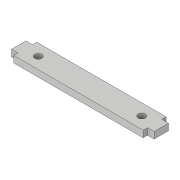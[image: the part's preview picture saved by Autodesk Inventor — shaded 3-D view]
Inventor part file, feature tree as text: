
AUTODESK INVENTOR PART (.ipt)
format: ipt  version: 2017 (Build 210142000, 142)  size: 99,328 bytes
history: native  units: in
note: dims shown in document units (in); Inventor stores cm internally (conversion verified against a paired STEP export)
features: extrude x2, sketch x2
ambient origin geometry x8: Origin, YZ Plane, XZ Plane, XY Plane, X Axis, Y Axis, Z Axis, Center Point
bodies: Solid1 (feature_tree)
feature tree (4):
  extrude  "Extrusion1"  Depth=0.4in
  extrude  "Extrusion2"  Depth=0.25in
  sketch  "Sketch1"  dims[d0=2.25in d1=0.4in]
  sketch  "Sketch2"  dims[d2=0.115in d3=0.25in d4=0.075in d5=0.7874in d7=2.365in d8=0.3937in d10=1.0in d12=0.115in d13=0.0in d14=0.125in d15=0.125in d16=0.2in d17=0.2in d18=1.8in d19=0.225in d20=0.115in d21=0.0in]
